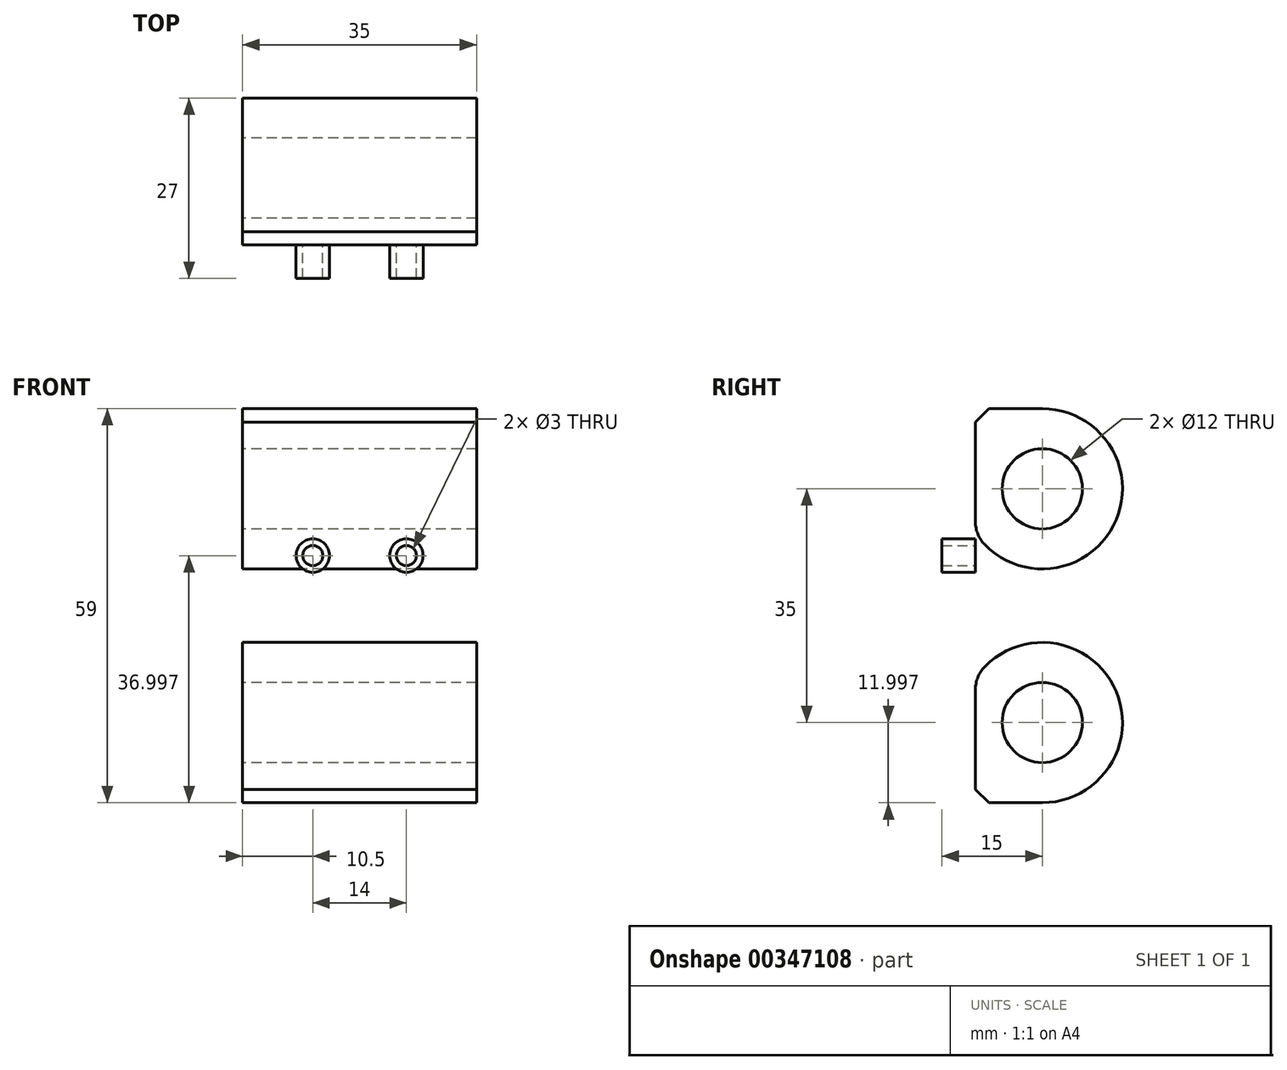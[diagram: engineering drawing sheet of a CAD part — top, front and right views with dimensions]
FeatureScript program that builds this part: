
annotation { "Feature Type Name" : "Feature", "Feature Type Description" : "" }
export const myFeature = defineFeature(function(context is Context, id is Id, definition is map)
    precondition{}
    {
        {
            var Q0;
            Q0=qCreatedBy(makeId("Right.planeOp"),FACE);
            var sketch = newSketch(context, id + "F0", { "sketchPlane" : qUnion([Q0])});
            skCircle(sketch, "E0", {"center": v(0, 34.13) * mm, "radius": 6 * mm});
            skLineSegment(sketch, "E1", {"start": v(0, 34.13) * mm, "end": v(0, -0.87) * mm});
            skCircle(sketch, "E2", {"center": v(0, -0.87) * mm, "radius": 6 * mm});
            skCircle(sketch, "E3", {"center": v(0, 34.13) * mm, "radius": 12 * mm});
            skCircle(sketch, "E4", {"center": v(0, -0.87) * mm, "radius": 12 * mm});
            skLineSegment(sketch, "E5", {"start": v(0, 34.13) * mm, "end": v(-6, 34.13) * mm});
            skLineSegment(sketch, "E6", {"start": v(0, 34.13) * mm, "end": v(0, -12.87) * mm});
            skLineSegment(sketch, "E7", {"start": v(0, -12.87) * mm, "end": v(-10, -12.87) * mm});
            skLineSegment(sketch, "E8", {"start": v(-10, -12.87) * mm, "end": v(-10, 46.13) * mm});
            skLineSegment(sketch, "E9", {"start": v(-10, 46.13) * mm, "end": v(0, 46.13) * mm});
            skSolve(sketch);
        }
        {
            var Q0;
            {var subQ0=sQuery(id+"F0.wireOp",EDGE,"E6");var subQ1=sQuery(id+"F0.wireOp",EDGE,"E2");var subQ2=makeQuery(id+"F0.imprint","INTERSECT",VERTEX,{"disambiguationData":[OD(0.0)],"derivedFrom":[subQ1,subQ0]});Q0=makeQuery(id+"F0.imprint","IMPRINT",FACE,{"disambiguationData":[TD([[makeQuery(id+"F0.imprint","IMPRINT",EDGE,{"disambiguationData":[TD([[subQ2,1.0]])],"derivedFrom":subQ1}),-1.0]])]});}
            var Q1;
            {var subQ0=sQuery(id+"F0.wireOp",EDGE,"E6");var subQ3=sQuery(id+"F0.wireOp",EDGE,"E2");var subQ4=makeQuery(id+"F0.imprint","INTERSECT",VERTEX,{"disambiguationData":[OD(0.0)],"derivedFrom":[subQ3,subQ0]});Q1=makeQuery(id+"F0.imprint","IMPRINT",FACE,{"disambiguationData":[TD([[makeQuery(id+"F0.imprint","IMPRINT",EDGE,{"disambiguationData":[TD([[subQ4,-1.0]])],"derivedFrom":subQ3}),-1.0]])]});}
            var Q2;
            {var subQ0=sQuery(id+"F0.wireOp",EDGE,"E7");Q2=makeQuery(id+"F0.imprint","IMPRINT",FACE,{"disambiguationData":[TD([[makeQuery(id+"F0.imprint","IMPRINT",EDGE,{"derivedFrom":subQ0}),-1.0]])]});}
            var Q3;
            {var subQ0=sQuery(id+"F0.wireOp",EDGE,"E6");var subQ1=sQuery(id+"F0.wireOp",EDGE,"E3");var subQ2=makeQuery(id+"F0.imprint","INTERSECT",VERTEX,{"derivedFrom":[subQ1,subQ0]});Q3=makeQuery(id+"F0.imprint","IMPRINT",FACE,{"disambiguationData":[TD([[makeQuery(id+"F0.imprint","IMPRINT",EDGE,{"disambiguationData":[TD([[subQ2,1.0]])],"derivedFrom":subQ1}),-1.0]])]});}
            var Q4;
            {var subQ7=sQuery(id+"F0.wireOp",EDGE,"E0");var subQ8=makeQuery(id+"F0.imprint","INTERSECT",VERTEX,{"derivedFrom":[subQ7,sQuery(id+"F0.wireOp",EDGE,"E5")]});Q4=makeQuery(id+"F0.imprint","IMPRINT",FACE,{"disambiguationData":[TD([[makeQuery(id+"F0.imprint","IMPRINT",EDGE,{"disambiguationData":[TD([[subQ8,-1.0]])],"derivedFrom":subQ7}),-1.0]])]});}
            var Q5;
            {var subQ0=sQuery(id+"F0.wireOp",EDGE,"E9");Q5=makeQuery(id+"F0.imprint","IMPRINT",FACE,{"disambiguationData":[TD([[makeQuery(id+"F0.imprint","IMPRINT",EDGE,{"derivedFrom":subQ0}),-1.0]])]});}
            extrude(context, id + "F1", {"entities" : qUnion([Q0, Q1, Q2, Q3, Q4, Q5]), "depth" : 35 * mm});
        }
        {
            var Q0;
            Q0=makeQuery(id+"F1.opExtrude","SWEPT_EDGE",EDGE,{"disambiguationData":[OSD([sQuery(id+"F0.wireOp",EDGE,"E1"),sQuery(id+"F0.wireOp",EDGE,"E3")])]});
            var Q1;
            Q1=makeQuery(id+"F1.opExtrude","SWEPT_EDGE",EDGE,{"disambiguationData":[OSD([sQuery(id+"F0.wireOp",EDGE,"E1"),sQuery(id+"F0.wireOp",EDGE,"E4")])]});
            fillet(context, id + "F2", {"entities" : qUnion([Q0, Q1]), "radius" : 5 * mm, "tangentPropagation" : true, "allowEdgeOverflow" : false});
        }
        {
            var Q0;
            Q0=makeQuery(id+"F1.opExtrude","SWEPT_EDGE",EDGE,{"disambiguationData":[OSD([sQuery(id+"F0.wireOp",EDGE,"E7"),sQuery(id+"F0.wireOp",EDGE,"E8")])]});
            var Q1;
            Q1=makeQuery(id+"F1.opExtrude","SWEPT_EDGE",EDGE,{"disambiguationData":[OSD([sQuery(id+"F0.wireOp",EDGE,"E8"),sQuery(id+"F0.wireOp",EDGE,"E9")])]});
            chamfer(context, id + "F3", {"entities" : qUnion([Q0, Q1]), "width" : 2 * mm, "tangentPropagation" : true});
        }
        {
            var Q0;
            Q0=makeQuery(id+"F1.opExtrude","SWEPT_FACE",FACE,{"disambiguationData":[OSD([sQuery(id+"F0.wireOp",EDGE,"E8")])]});
            var sketch = newSketch(context, id + "F4", { "sketchPlane" : qUnion([Q0])});
            skLineSegment(sketch, "E10", {"start": v(0, -10.87) * mm, "end": v(17.5, -10.87) * mm});
            skLineSegment(sketch, "E11", {"start": v(17.5, -10.87) * mm, "end": v(17.5, 24.13) * mm});
            skLineSegment(sketch, "E12", {"start": v(17.5, 24.13) * mm, "end": v(10.5, 24.13) * mm});
            skLineSegment(sketch, "E13", {"start": v(10.5, 24.13) * mm, "end": v(24.5, 24.13) * mm});
            skPoint(sketch, "E13.endSnap0", {"position": v(14, 24.13) * mm});
            skCircle(sketch, "E14", {"center": v(10.5, 24.13) * mm, "radius": 1.5 * mm});
            skCircle(sketch, "E15", {"center": v(24.5, 24.13) * mm, "radius": 1.5 * mm});
            skCircle(sketch, "E16", {"center": v(10.5, 24.13) * mm, "radius": 2.5 * mm});
            skCircle(sketch, "E17", {"center": v(24.5, 24.13) * mm, "radius": 2.5 * mm});
            skSolve(sketch);
        }
        {
            var Q0;
            Q0=makeQuery(id+"F4.imprint","IMPRINT",FACE,{"disambiguationData":[TD([[makeQuery(id+"F4.imprint","IMPRINT",EDGE,{"derivedFrom":sQuery(id+"F4.wireOp",EDGE,"E14")}),-1.0]])]});
            var Q1;
            Q1=makeQuery(id+"F4.imprint","IMPRINT",FACE,{"disambiguationData":[TD([[makeQuery(id+"F4.imprint","IMPRINT",EDGE,{"derivedFrom":sQuery(id+"F4.wireOp",EDGE,"E15")}),-1.0]])]});
            extrude(context, id + "F5", {"entities" : qUnion([Q0, Q1]), "operationType" : NewBodyOperationType.ADD, "depth" : 5 * mm});
        }
    });
